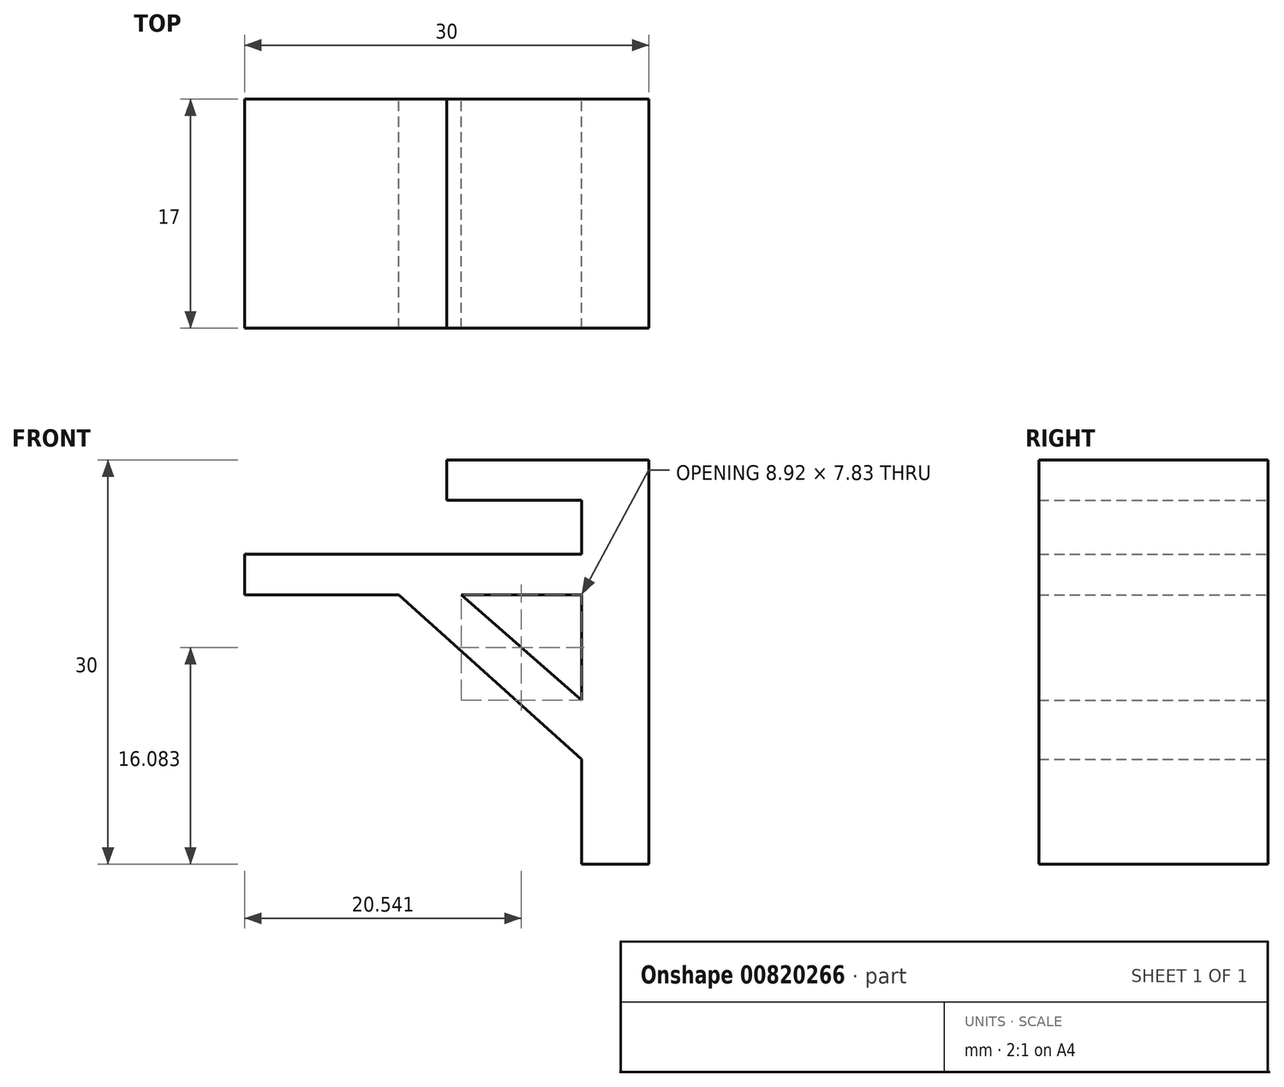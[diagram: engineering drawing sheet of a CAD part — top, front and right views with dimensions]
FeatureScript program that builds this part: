
annotation { "Feature Type Name" : "Feature", "Feature Type Description" : "" }
export const myFeature = defineFeature(function(context is Context, id is Id, definition is map)
    precondition{}
    {
        {
            var Q0;
            Q0=qCreatedBy(makeId("Front.planeOp"),FACE);
            var sketch = newSketch(context, id + "F0", { "sketchPlane" : qUnion([Q0])});
            skLineSegment(sketch, "E0.bottom", {"start": v(-10, 5.82) * mm, "end": v(0, 5.82) * mm});
            skLineSegment(sketch, "E0.top", {"start": v(-10, 2.82) * mm, "end": v(0, 2.82) * mm});
            skLineSegment(sketch, "E0.left", {"start": v(-10, 5.82) * mm, "end": v(-10, 2.82) * mm});
            skLineSegment(sketch, "E0.right", {"start": v(0, 5.82) * mm, "end": v(0, 2.82) * mm});
            skLineSegment(sketch, "E1.bottom", {"start": v(0, 5.82) * mm, "end": v(5, 5.82) * mm});
            skLineSegment(sketch, "E1.top", {"start": v(0, -1.18) * mm, "end": v(5, -1.18) * mm});
            skLineSegment(sketch, "E1.left", {"start": v(0, 5.82) * mm, "end": v(0, -1.18) * mm});
            skLineSegment(sketch, "E1.right", {"start": v(5, 5.82) * mm, "end": v(5, -1.18) * mm});
            skLineSegment(sketch, "E2.bottom", {"start": v(5, -1.18) * mm, "end": v(-25, -1.18) * mm});
            skLineSegment(sketch, "E2.top", {"start": v(5, -4.18) * mm, "end": v(-25, -4.18) * mm});
            skLineSegment(sketch, "E2.left", {"start": v(5, -1.18) * mm, "end": v(5, -4.18) * mm});
            skLineSegment(sketch, "E2.right", {"start": v(-25, -1.18) * mm, "end": v(-25, -4.18) * mm});
            skLineSegment(sketch, "E3.bottom", {"start": v(0, -4.18) * mm, "end": v(5, -4.18) * mm});
            skLineSegment(sketch, "E3.top", {"start": v(0, -24.18) * mm, "end": v(5, -24.18) * mm});
            skLineSegment(sketch, "E3.left", {"start": v(0, -4.18) * mm, "end": v(0, -24.18) * mm});
            skLineSegment(sketch, "E3.right", {"start": v(5, -4.18) * mm, "end": v(5, -24.18) * mm});
            skLineSegment(sketch, "E4", {"start": v(-13.57, -4.18) * mm, "end": v(0, -16.4) * mm});
            skLineSegment(sketch, "E5", {"start": v(0, -16.4) * mm, "end": v(0, -12.01) * mm});
            skLineSegment(sketch, "E6", {"start": v(0, -12.01) * mm, "end": v(-8.92, -4.18) * mm});
            skLineSegment(sketch, "E7", {"start": v(-8.92, -4.18) * mm, "end": v(-13.57, -4.18) * mm});
            skSolve(sketch);
        }
        {
            var Q0;
            Q0=makeQuery(id+"F0.imprint","IMPRINT",FACE,{"disambiguationData":[TD([[makeQuery(id+"F0.imprint","IMPRINT",EDGE,{"derivedFrom":sQuery(id+"F0.wireOp",EDGE,"E1.top")}),-1.0]])]});
            var Q1;
            {var subQ0=sQuery(id+"F0.wireOp",EDGE,"E4");Q1=makeQuery(id+"F0.imprint","IMPRINT",FACE,{"disambiguationData":[TD([[makeQuery(id+"F0.imprint","IMPRINT",EDGE,{"derivedFrom":subQ0}),1.0]])]});}
            var Q2;
            {var subQ1=sQuery(id+"F0.wireOp",EDGE,"E3.top");Q2=makeQuery(id+"F0.imprint","IMPRINT",FACE,{"disambiguationData":[TD([[makeQuery(id+"F0.imprint","IMPRINT",EDGE,{"derivedFrom":subQ1}),1.0]])]});}
            var Q3;
            Q3=makeQuery(id+"F0.imprint","IMPRINT",FACE,{"disambiguationData":[TD([[makeQuery(id+"F0.imprint","IMPRINT",EDGE,{"derivedFrom":sQuery(id+"F0.wireOp",EDGE,"E0.right")}),1.0]])]});
            var Q4;
            Q4=makeQuery(id+"F0.imprint","IMPRINT",FACE,{"disambiguationData":[TD([[makeQuery(id+"F0.imprint","IMPRINT",EDGE,{"derivedFrom":sQuery(id+"F0.wireOp",EDGE,"E0.bottom")}),-1.0]])]});
            extrude(context, id + "F1", {"entities" : qUnion([Q0, Q1, Q2, Q3, Q4]), "depth" : 17 * mm, "offsetDistance" : 25 * mm});
        }
    });
